# Revit family: Faucet-Two_Handle-American_Standard-Belmead-7426201_Series
name_source: partatom
category: Plumbing Fixtures
units: mm (PartAtom-declared; Revit-internal decimal feet)

## family parameters
Always vertical = No
Cut with Voids When Loaded = No
OmniClass Number = 23.45.55.17
OmniClass Title = Mixing Faucets
Part Type = Normal
Room Calculation Point = No
Round Connector Dimension = Use Diameter
Shared = Yes
Work Plane-Based = Yes

## types (3) — shared parameters
ADA Compliant = Yes
Assembly Code = D2020300
CW Connection = Yes
CWFU = 1.5
CalGreen Compliant = Yes
Cold Water Connection Diameter = 3/8"
Compliance Certifications = These products meet or exceed:ANSI A117.1, ASME A112.18.1, CSA B125.1, NSF/ANSI/CAN 61: Q≤1, NSF/ANSI 372
Default Elevation = 0"
Description = Belmeade Two-Handle 4-Inch Centerset Bathroom Faucet
Flow Rate = 1.2 gpm (4.5L/min)
HW Connection = Yes
HWFU = 1.5
Height = 7"
Hot Water Connection Diameter = 3/8"
Installation Type = Deck Mounted
Length = 9 3/4"
Manufacturer = American Standard
Pop Up Drain = Yes
Pop Up Drain Depth = 3"
Pop Up Drain Width = 5"
Product Documentation Link = https://lixil.cdn.celum.cloud
Product Page URL = https://www.americanstandard-us.com
URL = http://www.americanstandard-us.com
Vent Connection = No
Warranty Information = Limited Lifetime Warranty
Waste Connection = No
Waste Connection Diameter = 1 1/2"
Width = 4 7/8"
zero-valued in all types: WFU

## per-type parameters (varying)
| type | Finish | Material |
| 7426201.002 | Metal-American Standard-002-Polished Chrome | Metal-American Standard-002-Polished Chrome |
| 7426201.243 | Metal-American Standard-243-Matte Black | Metal-American Standard-243-Matte Black |
| 7426201.295 | Metal-American Standard-295-Brushed Nickel | Metal-American Standard-295-Brushed Nickel |

note: column(s) folded — value = type name in every type: Model

## geometry (parser evidence)
native form markers: Sweep x3
no freeform markers — native parametric forms only
